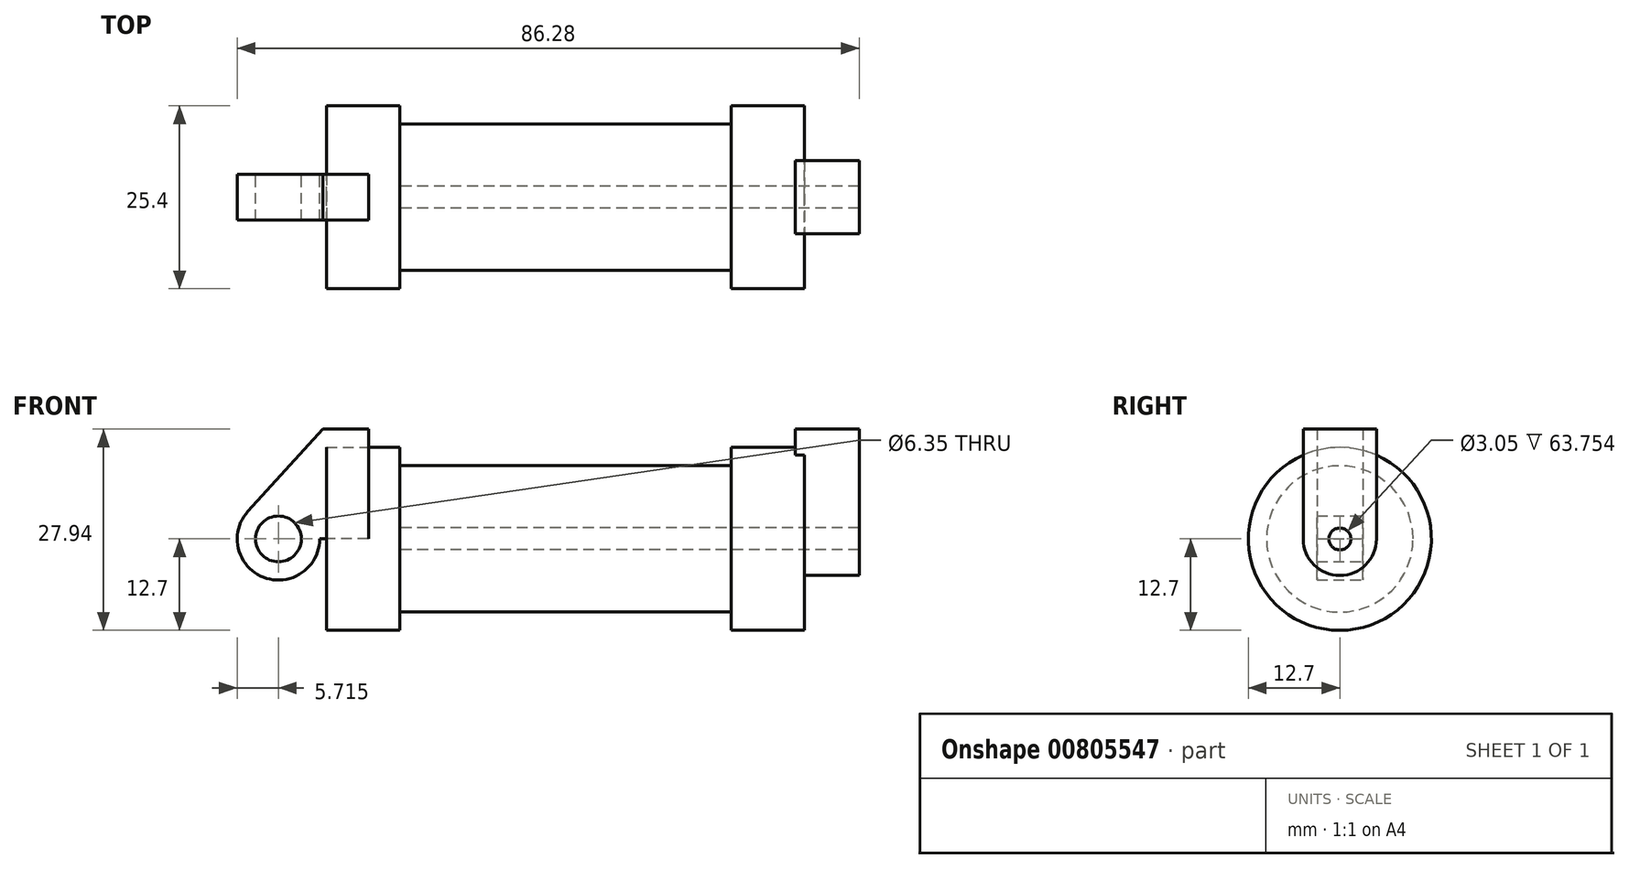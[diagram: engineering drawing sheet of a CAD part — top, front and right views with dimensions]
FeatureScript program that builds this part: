
annotation { "Feature Type Name" : "Feature", "Feature Type Description" : "" }
export const myFeature = defineFeature(function(context is Context, id is Id, definition is map)
    precondition{}
    {
        {
            var Q0;
            Q0=qCreatedBy(makeId("Front.planeOp"),FACE);
            var sketch = newSketch(context, id + "F0", { "sketchPlane" : qUnion([Q0])});
            skLineSegment(sketch, "E0", {"start": v(0, 0) * mm, "end": v(0, 12.7) * mm});
            skLineSegment(sketch, "E1", {"start": v(0, 12.7) * mm, "end": v(10.16, 12.7) * mm});
            skLineSegment(sketch, "E2", {"start": v(10.16, 12.7) * mm, "end": v(10.16, 10.16) * mm});
            skLineSegment(sketch, "E3", {"start": v(10.16, 10.16) * mm, "end": v(56.13, 10.16) * mm});
            skLineSegment(sketch, "E4", {"start": v(56.13, 10.16) * mm, "end": v(56.13, 12.7) * mm});
            skLineSegment(sketch, "E5", {"start": v(56.13, 12.7) * mm, "end": v(66.3, 12.7) * mm});
            skLineSegment(sketch, "E6", {"start": v(66.3, 12.7) * mm, "end": v(66.3, 0) * mm});
            skLineSegment(sketch, "E7", {"start": v(66.3, 0) * mm, "end": v(0, 0) * mm});
            skLineSegment(sketch, "E8", {"start": v(5.84, 15.24) * mm, "end": v(-0.5, 15.24) * mm});
            skLineSegment(sketch, "E9", {"start": v(-0.5, 15.24) * mm, "end": v(-10.88, 3.85) * mm});
            skLineSegment(sketch, "E10", {"start": v(0, 0) * mm, "end": v(-6.65, 0) * mm});
            skCircle(sketch, "E11", {"center": v(-6.65, 0) * mm, "radius": 5.72 * mm});
            skCircle(sketch, "E12", {"center": v(-6.65, 0) * mm, "radius": 3.18 * mm});
            skLineSegment(sketch, "E13", {"start": v(5.84, 15.24) * mm, "end": v(5.84, -9.4) * mm});
            skLineSegment(sketch, "E14", {"start": v(5.84, -9.4) * mm, "end": v(-8.18, -5.5) * mm});
            skSolve(sketch);
        }
        {
            var Q0;
            {var subQ0=sQuery(id+"F0.wireOp",EDGE,"E2");Q0=makeQuery(id+"F0.imprint","IMPRINT",FACE,{"disambiguationData":[TD([[makeQuery(id+"F0.imprint","IMPRINT",EDGE,{"derivedFrom":subQ0}),-1.0]])]});}
            var Q1;
            {var subQ0=sQuery(id+"F0.wireOp",EDGE,"E0");Q1=makeQuery(id+"F0.imprint","IMPRINT",FACE,{"disambiguationData":[TD([[makeQuery(id+"F0.imprint","IMPRINT",EDGE,{"derivedFrom":subQ0}),-1.0]])]});}
            var Q2;
            Q2=sQuery(id+"F0.wireOp",EDGE,"E7");
            revolve(context, id + "F1", {"surfaceOperationType" : NewSurfaceOperationType.NEW, "entities" : qUnion([Q0, Q1]), "axis" : qUnion([Q2]), "revolveType" : RevolveType.FULL});
        }
        {
            var Q0;
            {var subQ0=sQuery(id+"F0.wireOp",EDGE,"E0");Q0=makeQuery(id+"F0.imprint","IMPRINT",FACE,{"disambiguationData":[TD([[makeQuery(id+"F0.imprint","IMPRINT",EDGE,{"derivedFrom":subQ0}),-1.0]])]});}
            var Q1;
            {var subQ5=sQuery(id+"F0.wireOp",EDGE,"E12");Q1=makeQuery(id+"F0.imprint","IMPRINT",FACE,{"disambiguationData":[TD([[makeQuery(id+"F0.imprint","IMPRINT",EDGE,{"derivedFrom":subQ5}),-1.0]])]});}
            var Q2;
            {var subQ1=sQuery(id+"F0.wireOp",EDGE,"E0");Q2=makeQuery(id+"F0.imprint","IMPRINT",FACE,{"disambiguationData":[TD([[makeQuery(id+"F0.imprint","IMPRINT",EDGE,{"derivedFrom":subQ1}),1.0]])]});}
            extrude(context, id + "F2", {"entities" : qUnion([Q0, Q1, Q2]), "endBound" : BoundingType.SYMMETRIC, "depth" : 6.35 * mm, "offsetDistance" : 25.4 * mm});
        }
        {
            var Q0;
            Q0=makeQuery(id+"F1.opRevolve","SWEPT_FACE",FACE,{"disambiguationData":[OSD([sQuery(id+"F0.wireOp",EDGE,"E6")])]});
            var sketch = newSketch(context, id + "F3", { "sketchPlane" : qUnion([Q0])});
            skCircle(sketch, "E15", {"center": v(0, 0) * mm, "radius": 1.52 * mm});
            skCircle(sketch, "E16", {"center": v(0, 0) * mm, "radius": 5.08 * mm});
            skLineSegment(sketch, "E17", {"start": v(5.08, 0) * mm, "end": v(5.08, 15.24) * mm});
            skLineSegment(sketch, "E18", {"start": v(-5.08, 0) * mm, "end": v(-5.08, 15.24) * mm});
            skLineSegment(sketch, "E19", {"start": v(-5.08, 15.24) * mm, "end": v(5.08, 15.24) * mm});
            skSolve(sketch);
        }
        {
            var Q0;
            {var subQ0=sQuery(id+"F3.wireOp",EDGE,"E17");var subQ1=sQuery(id+"F3.wireOp",EDGE,"E16");var subQ2=makeQuery(id+"F3.imprint","INTERSECT",VERTEX,{"derivedFrom":[subQ1,subQ0]});Q0=makeQuery(id+"F3.imprint","IMPRINT",FACE,{"disambiguationData":[TD([[makeQuery(id+"F3.imprint","IMPRINT",EDGE,{"disambiguationData":[TD([[subQ2,-1.0]])],"derivedFrom":subQ1}),-1.0]])]});}
            var Q1;
            {var subQ0=sQuery(id+"F3.wireOp",EDGE,"E19");Q1=makeQuery(id+"F3.imprint","IMPRINT",FACE,{"disambiguationData":[TD([[makeQuery(id+"F3.imprint","IMPRINT",EDGE,{"derivedFrom":subQ0}),-1.0]])]});}
            var Q2;
            Q2=makeQuery(id+"F3.imprint","IMPRINT",FACE,{"disambiguationData":[TD([[makeQuery(id+"F3.imprint","IMPRINT",EDGE,{"derivedFrom":sQuery(id+"F3.wireOp",EDGE,"E15")}),-1.0]])]});
            extrude(context, id + "F4", {"entities" : qUnion([Q0, Q1, Q2]), "operationType" : NewBodyOperationType.ADD, "depth" : 7.62 * mm, "offsetDistance" : 25.4 * mm, "hasSecondDirection" : true, "secondDirectionOppositeDirection" : true, "secondDirectionDepth" : 1.27 * mm});
        }
        {
            var Q0;
            Q0=makeQuery(id+"F4.boolean.opBoolean","SPLIT",FACE,{"disambiguationData":[TD([makeQuery(id+"F4.opExtrude","SWEPT_FACE",FACE,{"disambiguationData":[OSD([sQuery(id+"F3.wireOp",EDGE,"E15")])]})])],"derivedFrom":makeQuery(id+"F1.opRevolve","SWEPT_FACE",FACE,{"disambiguationData":[OSD([sQuery(id+"F0.wireOp",EDGE,"E6")])]})});
            var Q1;
            Q1=makeQuery(id+"F1.opRevolve","SWEPT_FACE",FACE,{"disambiguationData":[OSD([sQuery(id+"F0.wireOp",EDGE,"E2")])]});
            extrude(context, id + "F5", {"entities" : qUnion([Q0]), "operationType" : NewBodyOperationType.REMOVE, "endBound" : BoundingType.UP_TO_SURFACE, "oppositeDirection" : true, "depth" : 25.4 * mm, "endBoundEntityFace" : qUnion([Q1]), "offsetDistance" : 25.4 * mm});
        }
    });
